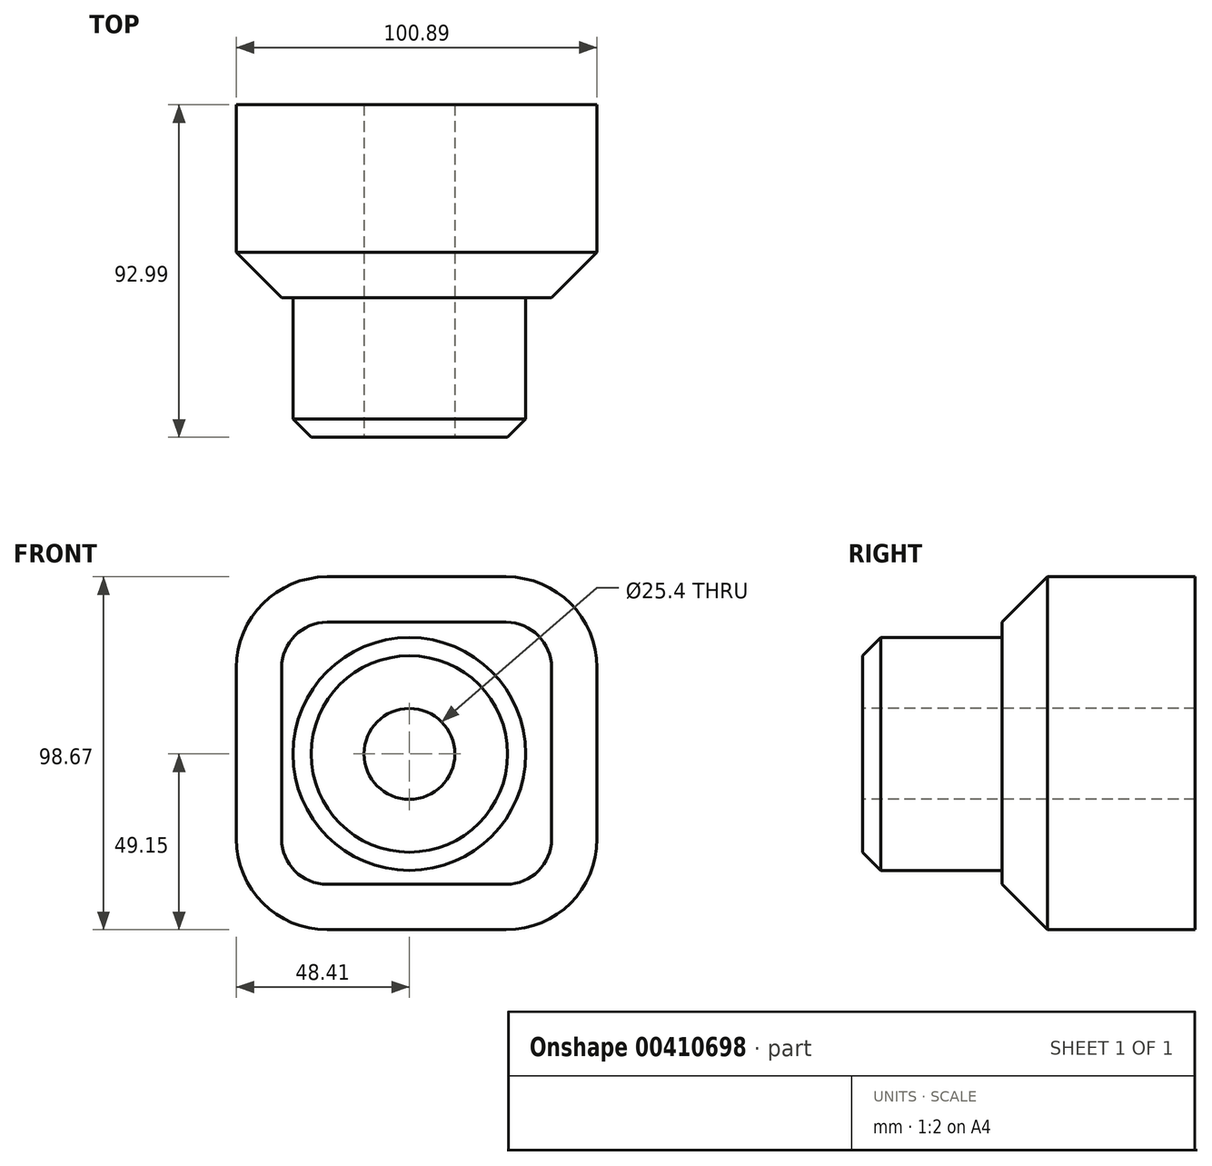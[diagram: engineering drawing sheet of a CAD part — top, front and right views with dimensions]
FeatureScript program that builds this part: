
annotation { "Feature Type Name" : "Feature", "Feature Type Description" : "" }
export const myFeature = defineFeature(function(context is Context, id is Id, definition is map)
    precondition{}
    {
        {
            var Q0;
            Q0=qCreatedBy(makeId("Front.planeOp"),FACE);
            var sketch = newSketch(context, id + "F0", { "sketchPlane" : qUnion([Q0])});
            skLineSegment(sketch, "E0.bottom", {"start": v(52.48, 49.52) * mm, "end": v(-48.41, 49.52) * mm});
            skLineSegment(sketch, "E0.top", {"start": v(52.48, -49.15) * mm, "end": v(-48.41, -49.15) * mm});
            skLineSegment(sketch, "E0.left", {"start": v(52.48, 49.52) * mm, "end": v(52.48, -49.15) * mm});
            skLineSegment(sketch, "E0.right", {"start": v(-48.41, 49.52) * mm, "end": v(-48.41, -49.15) * mm});
            skSolve(sketch);
        }
        {
            var Q0;
            Q0 = qSketchRegion(id + "F0", true);
            extrude(context, id + "F1", {"entities" : qUnion([Q0]), "depth" : 53.98 * mm});
        }
        {
            var Q0;
            Q0=makeQuery(id+"F1.opExtrude","SWEPT_EDGE",EDGE,{"disambiguationData":[OSD([sQuery(id+"F0.wireOp",EDGE,"E0.bottom"),sQuery(id+"F0.wireOp",EDGE,"E0.left")])]});
            var Q1;
            Q1=makeQuery(id+"F1.opExtrude","SWEPT_EDGE",EDGE,{"disambiguationData":[OSD([sQuery(id+"F0.wireOp",EDGE,"E0.top"),sQuery(id+"F0.wireOp",EDGE,"E0.left")])]});
            var Q2;
            Q2=makeQuery(id+"F1.opExtrude","SWEPT_EDGE",EDGE,{"disambiguationData":[OSD([sQuery(id+"F0.wireOp",EDGE,"E0.top"),sQuery(id+"F0.wireOp",EDGE,"E0.right")])]});
            var Q3;
            Q3=makeQuery(id+"F1.opExtrude","SWEPT_EDGE",EDGE,{"disambiguationData":[OSD([sQuery(id+"F0.wireOp",EDGE,"E0.bottom"),sQuery(id+"F0.wireOp",EDGE,"E0.right")])]});
            fillet(context, id + "F2", {"entities" : qUnion([Q0, Q1, Q2, Q3]), "radius" : 25.4 * mm, "tangentPropagation" : true, "allowEdgeOverflow" : false});
        }
        {
            var Q0;
            Q0=makeQuery(id+"F1.opExtrude","CAP_FACE",FACE,{"disambiguationData":[OSD([sQuery(id+"F0.wireOp",EDGE,"E0.bottom"),sQuery(id+"F0.wireOp",EDGE,"E0.top"),sQuery(id+"F0.wireOp",EDGE,"E0.left"),sQuery(id+"F0.wireOp",EDGE,"E0.right")])],"isStart":false});
            var sketch = newSketch(context, id + "F3", { "sketchPlane" : qUnion([Q0])});
            skCircle(sketch, "E1", {"center": v(0, 0) * mm, "radius": 32.54 * mm});
            skSolve(sketch);
        }
        {
            var Q0;
            Q0=makeQuery(id+"F3.imprint","IMPRINT",FACE,{"disambiguationData":[TD([[makeQuery(id+"F3.imprint","IMPRINT",EDGE,{"derivedFrom":sQuery(id+"F3.wireOp",EDGE,"E1")}),1.0]])]});
            var Q1;
            Q1 = qSketchRegion(id + "F3", true);
            extrude(context, id + "F4", {"entities" : qUnion([Q0, Q1]), "operationType" : NewBodyOperationType.ADD, "depth" : 39 * mm});
        }
        {
            var Q0;
            Q0=makeQuery(id+"F4.opExtrude","CAP_FACE",FACE,{"disambiguationData":[OSD([sQuery(id+"F3.wireOp",EDGE,"E1")])],"isStart":false});
            var sketch = newSketch(context, id + "F5", { "sketchPlane" : qUnion([Q0])});
            skPoint(sketch, "E2", {"position": v(0, 0) * mm});
            skSolve(sketch);
        }
        {
            var Q0;
            Q0=sQuery(id+"F5.wireOp",VERTEX,"E2");
            var Q1;
            Q1=makeQuery(id+"F1.opExtrude","SWEPT_BODY",BODY,{"disambiguationData":[OSD([sQuery(id+"F0.wireOp",EDGE,"E0.bottom"),sQuery(id+"F0.wireOp",EDGE,"E0.top"),sQuery(id+"F0.wireOp",EDGE,"E0.left"),sQuery(id+"F0.wireOp",EDGE,"E0.right")])]});
            hole(context, id + "F6", {"style" : HoleStyle.SIMPLE, "endStyle" : HoleEndStyle.THROUGH, "holeDiameter" : 25.4 * mm, "isTappedThrough" : true, "tappedDepth" : 12.7 * mm, "tapClearance" : 3, "locations" : qUnion([Q0]), "scope" : qUnion([Q1])});
        }
        {
            var Q0;
            Q0=makeQuery(id+"F1.opExtrude","CAP_EDGE",EDGE,{"disambiguationData":[OSD([sQuery(id+"F0.wireOp",EDGE,"E0.right")])],"isStart":false});
            chamfer(context, id + "F7", {"entities" : qUnion([Q0]), "width" : 12.7 * mm, "tangentPropagation" : true});
        }
        {
            var Q0;
            Q0=makeQuery(id+"F4.opExtrude","CAP_EDGE",EDGE,{"disambiguationData":[OSD([sQuery(id+"F3.wireOp",EDGE,"E1")])],"isStart":false});
            chamfer(context, id + "F8", {"entities" : qUnion([Q0]), "width" : 5.08 * mm, "tangentPropagation" : true});
        }
    });
